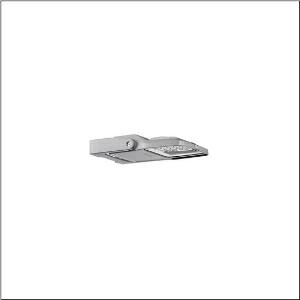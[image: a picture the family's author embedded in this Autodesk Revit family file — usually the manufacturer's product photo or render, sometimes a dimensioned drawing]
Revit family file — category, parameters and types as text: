
# Revit family: floodlight_fl_21_iq_micro___pl43_5xa7761a2a2a_4945
name_source: partatom
category: Lighting Fixtures
units: mm (PartAtom-declared; Revit-internal decimal feet)

## family parameters
Cut with Voids When Loaded = No
Host = Face
Light Source = No
Part Type = Normal
Room Calculation Point = No
Round Connector Dimension = Use Diameter
Shared = No

## types (1)
- --- (1 x LED, 3040 lm, 23.1 W, 3000K)
    Apparent Load = 23 VA
    CIE Flux Codes = 29 80 99 100 100
    Color Rendering = 70
    Color Temperature = 3000K
    Default Elevation = 1800 mm
    Description = Floodlight FL 21 iQ micro, floodlight, primary light control with lens, of PMMA, primary optical cover: protective disc, of toughened safety glass, transparent, light distribution: PL43, light emission: direct distribution, installation type: surface-mounted, LED, High Power LED, rated luminous flux: 3.040lm, luminous efficacy: 132lm/W, light colour: 730, colour temperature: 3000K, control: optimised constant luminous flux control (CLO 2.0), Desk-Remote (wireless, voltage-free reading and setting of iQ features in the workshop via application-optimized NFC function/RFID function), Light-Fading, Smart-Wire, Night-Set, Lumen-Switch, Temp-Guard, Auto-Match, with terminal, 6-pole, mains connection: 220..240V, AC, 50/60Hz, start of lifetime: 23W, end of service life: 24W, reduction: 11W, luminaire housing, of diecast aluminium, powder-coated, Siteco® metallic grey (DB 702S), corrosivity category C5 mid according to DIN EN ISO 12944, sealing non-destructively replaceable, design bracket, of diecast aluminium, powder-coated, Siteco® metallic grey (DB 702S), protection rating (complete): IP66, insulation class (complete): insulation class II (safety insulation), certification: CE, ENEC, VDE, protection symbol: D, impact resistance: IK07, permissible operating ambient temperature: -40..+40°C, permissible operating ambient temperature for outdoor applications: -40..+50°C, standard: DIN EN 12944, LABS conformity tested according to VDMA 24364:2018-05, packaging unit: 1 piece

Light Distribution: PL43
    Height = 65 mm
    Lamp = 1 x LED
    Lamp Light Flux = 3040 lm
    Lamp Power = 23.1 W
    Lamp count = 1
    Length = 312 mm
    Luminous efficacy = 132 lm/W
    Manufacturer = Siteco
    ModVariant = No
    Model = 5XA7761A2A2A
    Mounting Place = Wall
    Mounting Type = Surface mounted
    Number of Poles = 1
    OnlyDefault = Yes
    Power Factor = 1
    Product Name = Floodlight FL 21 iQ micro | PL43
    Product group = floodlight | wall mounted
    ProductGroupID = 2001
    Protection Class = Protection class II
    Protection Degree = IP 66
    RLX_Detail_Level = 1
    RLX_Emergency_Light_Flux = 0 lm
    RLX_Emergency_Type = 0
    RLX_Emergency_Type_DB = No
    RlxData = <blob elided: 97933 chars, md5=7db22656>
    Socket = socket
    Standby Power = 0 W
    System Light Flux = 3040 lm
    System Power = 23 W
    Type Comments = factory setting: luminous flux: 100 % | dim-lin: 254 | 455 mA
    Type Image = l_1006878.jpg
    URL = http://relux.com
    VarID = @adj_110237
    Voltage = 0 V
    Weight = 0.00 kg
    Width = 230 mm

## geometry (parser evidence)
native form markers: Blend x4, Sweep x11
no freeform markers — native parametric forms only
